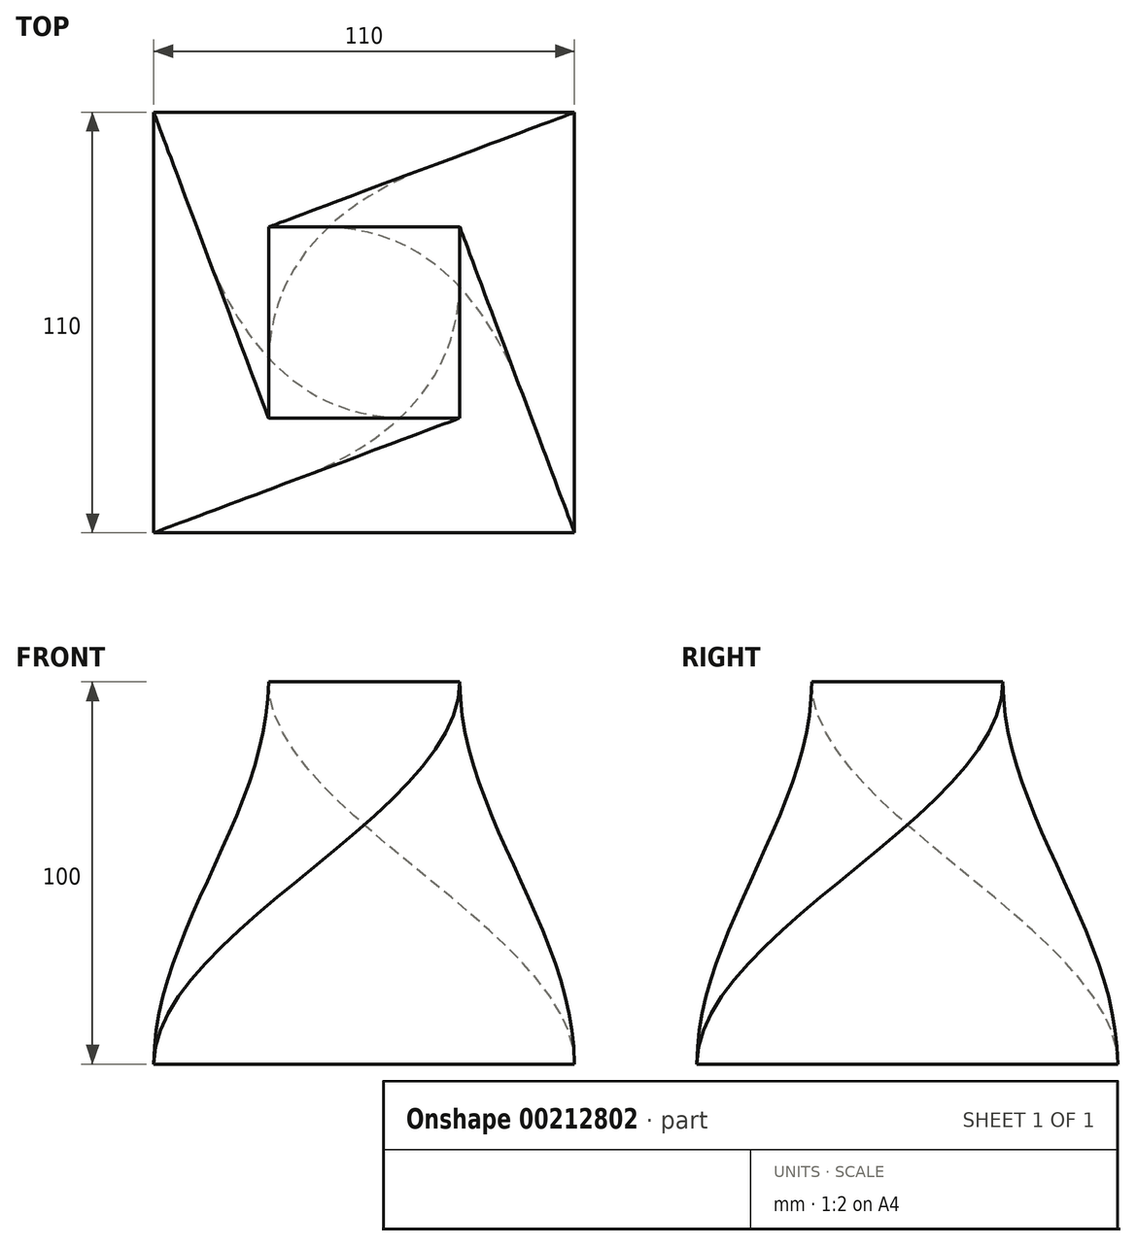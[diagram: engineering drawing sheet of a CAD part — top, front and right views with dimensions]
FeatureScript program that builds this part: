
annotation { "Feature Type Name" : "Feature", "Feature Type Description" : "" }
export const myFeature = defineFeature(function(context is Context, id is Id, definition is map)
    precondition{}
    {
        {
            var Q0;
            Q0=qCreatedBy(makeId("Top.planeOp"),FACE);
            var sketch = newSketch(context, id + "F0", { "sketchPlane" : qUnion([Q0])});
            skLineSegment(sketch, "E0.bottom", {"start": v(25, -25) * mm, "end": v(-25, -25) * mm});
            skLineSegment(sketch, "E0.top", {"start": v(25, 25) * mm, "end": v(-25, 25) * mm});
            skLineSegment(sketch, "E0.left", {"start": v(25, -25) * mm, "end": v(25, 25) * mm});
            skLineSegment(sketch, "E0.right", {"start": v(-25, -25) * mm, "end": v(-25, 25) * mm});
            skPoint(sketch, "E0.middle", {"position": v(0, 0) * mm});
            skSolve(sketch);
        }
        {
            var Q0;
            Q0=qCreatedBy(makeId("Top.planeOp"),FACE);
            cPlane(context, id + "F1", {"entities" : qUnion([Q0]), "cplaneType" : CPlaneType.OFFSET, "offset" : 100 * mm, "oppositeDirection" : true, "width" : 150 * mm, "height" : 150 * mm});
        }
        {
            var Q0;
            Q0=qCreatedBy(id+"F1.planeOp",FACE);
            var sketch = newSketch(context, id + "F2", { "sketchPlane" : qUnion([Q0])});
            skLineSegment(sketch, "E1.bottom", {"start": v(55, -55) * mm, "end": v(-55, -55) * mm});
            skLineSegment(sketch, "E1.top", {"start": v(55, 55) * mm, "end": v(-55, 55) * mm});
            skLineSegment(sketch, "E1.left", {"start": v(55, -55) * mm, "end": v(55, 55) * mm});
            skLineSegment(sketch, "E1.right", {"start": v(-55, -55) * mm, "end": v(-55, 55) * mm});
            skPoint(sketch, "E1.middle", {"position": v(0, 0) * mm});
            skSolve(sketch);
        }
        {
            var Q0;
            Q0=makeQuery(id+"F2.imprint","IMPRINT",FACE,{"disambiguationData":[TD([[makeQuery(id+"F2.imprint","IMPRINT",EDGE,{"derivedFrom":sQuery(id+"F2.wireOp",EDGE,"E1.bottom")}),-1.0]])]});
            var Q1;
            Q1=makeQuery(id+"F0.imprint","IMPRINT",FACE,{"disambiguationData":[TD([[makeQuery(id+"F0.imprint","IMPRINT",EDGE,{"derivedFrom":sQuery(id+"F0.wireOp",EDGE,"E0.bottom")}),-1.0]])]});
            var Q2;
            Q2=sQuery(id+"F2.wireOp",VERTEX,"E1.right.start");
            var Q3;
            Q3=sQuery(id+"F0.wireOp",VERTEX,"E0.bottom.start");
            loft(context, id + "F3", {"startCondition" : LoftEndDerivativeType.NORMAL_TO_PROFILE, "startMagnitude" : 1, "endCondition" : LoftEndDerivativeType.NORMAL_TO_PROFILE, "endMagnitude" : 1, "sheetProfilesArray" : [{ "sheetProfileEntities" : qUnion([Q0]) }, { "sheetProfileEntities" : qUnion([Q1]) }], "matchConnections" : true, "connections" : [{ "connectionEntities" : qUnion([Q2, Q3]), "connectionEdgeQueries" : qUnion([]), "connectionEdgeParameters" : [] }]});
        }
    });
